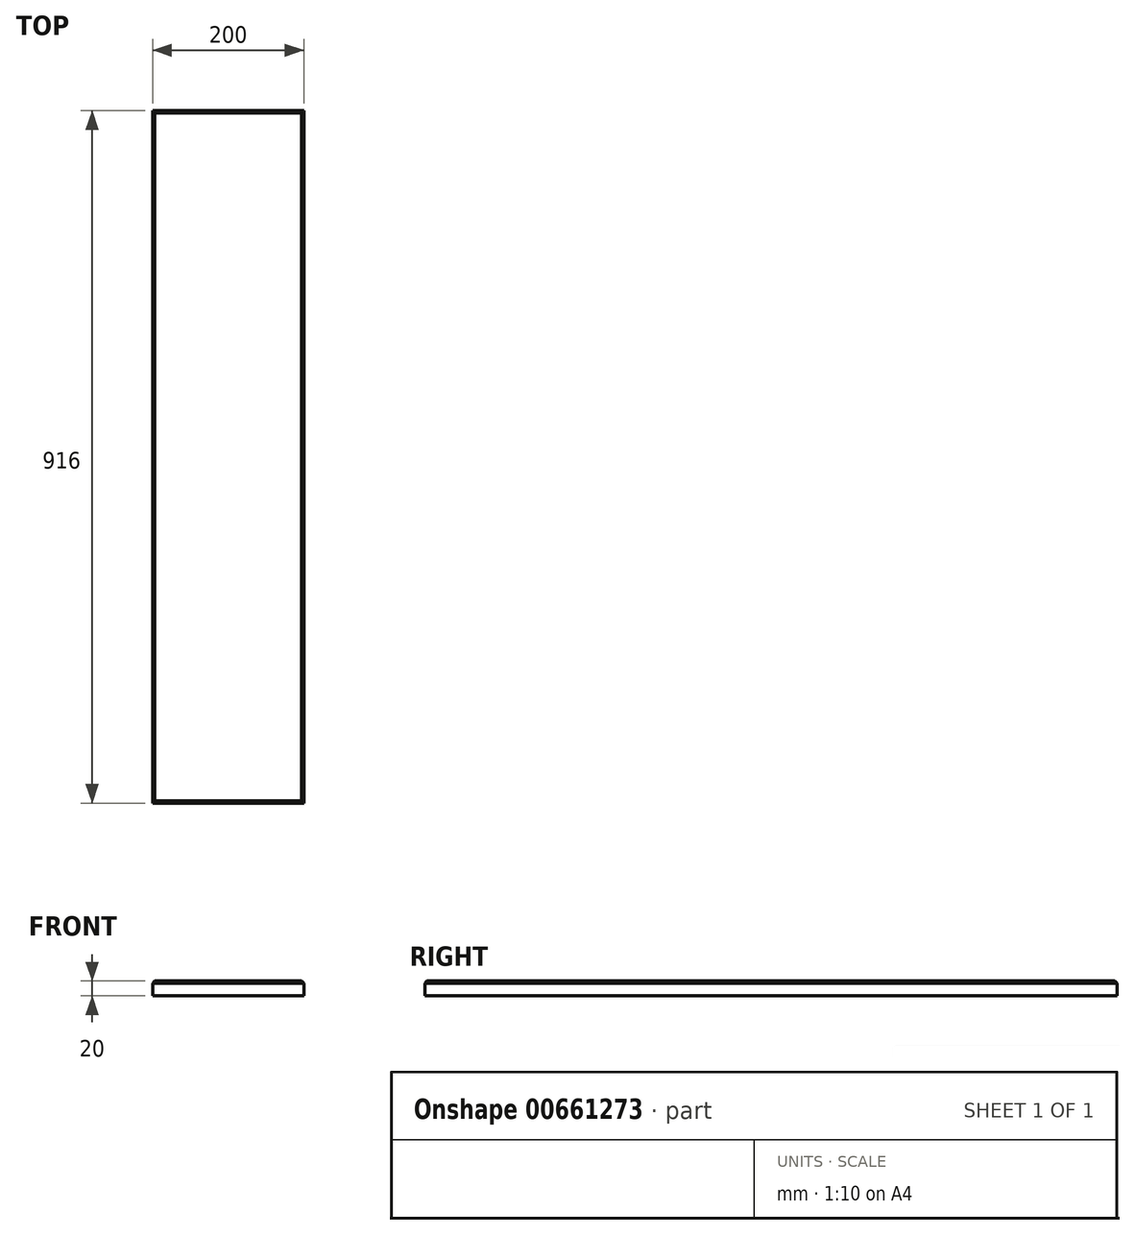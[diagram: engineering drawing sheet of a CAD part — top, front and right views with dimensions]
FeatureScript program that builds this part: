
annotation { "Feature Type Name" : "Feature", "Feature Type Description" : "" }
export const myFeature = defineFeature(function(context is Context, id is Id, definition is map)
    precondition{}
    {
        {
            var Q0;
            Q0=qCreatedBy(makeId("Front.planeOp"),FACE);
            var sketch = newSketch(context, id + "F0", { "sketchPlane" : qUnion([Q0])});
            skLineSegment(sketch, "E0.bottom", {"start": v(-100, 10) * mm, "end": v(100, 10) * mm});
            skLineSegment(sketch, "E0.top", {"start": v(-100, -10) * mm, "end": v(100, -10) * mm});
            skLineSegment(sketch, "E0.left", {"start": v(-100, 10) * mm, "end": v(-100, -10) * mm});
            skLineSegment(sketch, "E0.right", {"start": v(100, 10) * mm, "end": v(100, -10) * mm});
            skPoint(sketch, "E0.middle", {"position": v(0, 0) * mm});
            skSolve(sketch);
        }
        {
            var Q0;
            Q0 = qSketchRegion(id + "F0", true);
            extrude(context, id + "F1", {"entities" : qUnion([Q0]), "endBound" : BoundingType.SYMMETRIC, "depth" : 916 * mm, "offsetDistance" : 25 * mm});
        }
        {
            var Q0;
            Q0=makeQuery(id+"F1.opExtrude","SWEPT_EDGE",EDGE,{"disambiguationData":[OSD([sQuery(id+"F0.wireOp",EDGE,"E0.bottom"),sQuery(id+"F0.wireOp",EDGE,"E0.right")])]});
            var Q1;
            Q1=makeQuery(id+"F1.opExtrude","SWEPT_EDGE",EDGE,{"disambiguationData":[OSD([sQuery(id+"F0.wireOp",EDGE,"E0.bottom"),sQuery(id+"F0.wireOp",EDGE,"E0.left")])]});
            var Q2;
            Q2=makeQuery(id+"F1.opExtrude","CAP_EDGE",EDGE,{"disambiguationData":[OSD([sQuery(id+"F0.wireOp",EDGE,"E0.bottom")])],"isStart":false});
            var Q3;
            Q3=makeQuery(id+"F1.opExtrude","CAP_EDGE",EDGE,{"disambiguationData":[OSD([sQuery(id+"F0.wireOp",EDGE,"E0.bottom")])],"isStart":true});
            chamfer(context, id + "F2", {"entities" : qUnion([Q0, Q1, Q2, Q3]), "width" : 3 * mm, "tangentPropagation" : true});
        }
    });
